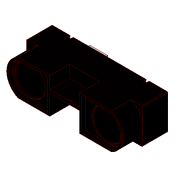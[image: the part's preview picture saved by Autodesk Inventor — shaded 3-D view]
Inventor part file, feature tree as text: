
AUTODESK INVENTOR PART (.ipt)
format: ipt  version: 2016 (Build 200138000, 138)  size: 363,008 bytes
history: native  units: in
note: dims shown in document units (in); Inventor stores cm internally (conversion verified against a paired STEP export)
features: sketch x12, extrude x11, projected_geometry x8, plane x2, revolve x1, mirror x1, chamfer x1, fillet x1
ambient origin geometry x8: Origin, YZ Plane, XZ Plane, XY Plane, X Axis, Y Axis, Z Axis, Center Point
bodies: Solid1 (feature_tree)
feature tree (37):
  extrude  "Extrusion1"  Depth=0.695in
  extrude  "Extrusion2"  Depth=0.035in
  extrude  "Extrusion3"  Depth=0.06in
  extrude  "Extrusion4"  Depth=0.365in
  extrude  "Extrusion5"  Depth=0.05in
  extrude  "Extrusion6"  Depth=0.07in TaperAngle=0.0deg
  plane  "Work Plane1"
  revolve  "Revolution1"  [1 undecoded]
  plane  "Work Plane2"
  mirror  "Mirror1"
  extrude  "Extrusion7"  Depth=0.85in
  extrude  "Extrusion8"  Depth=0.24in
  extrude  "Extrusion9"  Depth=0.39in
  extrude  "Extrusion10"  Depth=0.075in TaperAngle=0.0deg
  extrude  "Extrusion11"  Depth=0.0156in
  chamfer  "Chamfer1"  Distance=0.12in
  fillet  "Fillet1"  [1 undecoded]
  sketch  "Sketch1"  dims[d0=2.285in d1=0.695in]
  sketch  "Sketch2"  dims[d2=0.495in d3=0.0in d4=0.035in]
  projected_geometry  "Projected Loop1"
  sketch  "Sketch3"  dims[d5=0.07in d6=0.0in d7=0.06in]
  projected_geometry  "Projected Loop2"
  sketch  "Sketch4"  dims[d8=0.06in d9=0.365in]
  sketch  "Sketch5"  dims[d10=0.365in d11=0.05in]
  projected_geometry  "Projected Loop3"
  sketch  "Sketch6"  dims[d12=0.05in d13=0.07in d14=0.0in]
  projected_geometry  "Projected Loop4"
  projected_geometry  "Projected Loop5"
  sketch  "Sketch7"  dims[d17=0.625in d18=0.625in]
  projected_geometry  "Projected Loop6"
  sketch  "Sketch8"  dims[d19=0.85in d20=0.85in]
  projected_geometry  "Projected Loop7"
  sketch  "Sketch9"  dims[d21=0.06in d22=0.24in]
  sketch  "Sketch10"  dims[d23=0.39in d24=0.0in d25=0.04in]
  projected_geometry  "Projected Loop8"
  sketch  "Sketch11"  dims[d26=0.04in d27=0.075in d28=0.0in]
  sketch  "Sketch12"  dims[d29=0.59in d30=0.59in d31=0.12in d32=0.0in d33=-0.3475in d34=0.0in d35=0.0in d36=0.0312in d37=90.0deg d38=-1.1425in d39=0.165in d40=0.08in d41=0.04in d43=0.2in d44=0.075in d45=0.0in d46=0.35in d47=0.135in d48=0.08in d49=0.645in d50=0.18in d51=0.0in d52=0.015in d53=0.165in d54=0.0in d56=0.035in d57=0.065in d58=0.055in d59=0.165in d60=0.0in d61=0.02in d62=0.02in d63=0.0367in d64=0.0367in d65=0.0367in d66=0.0367in d67=0.0367in d68=0.0367in d69=0.0075in d70=0.0075in d72=0.0367in d73=0.15in d74=0.0in d75=0.0104in d76=0.125in d77=45.0deg d78=0.0156in]
note: 2 required parameter values undecoded (feature->parameter linkage not recoverable at this tier; creation-order binding heuristic only, values carry confidence <= 0.55)